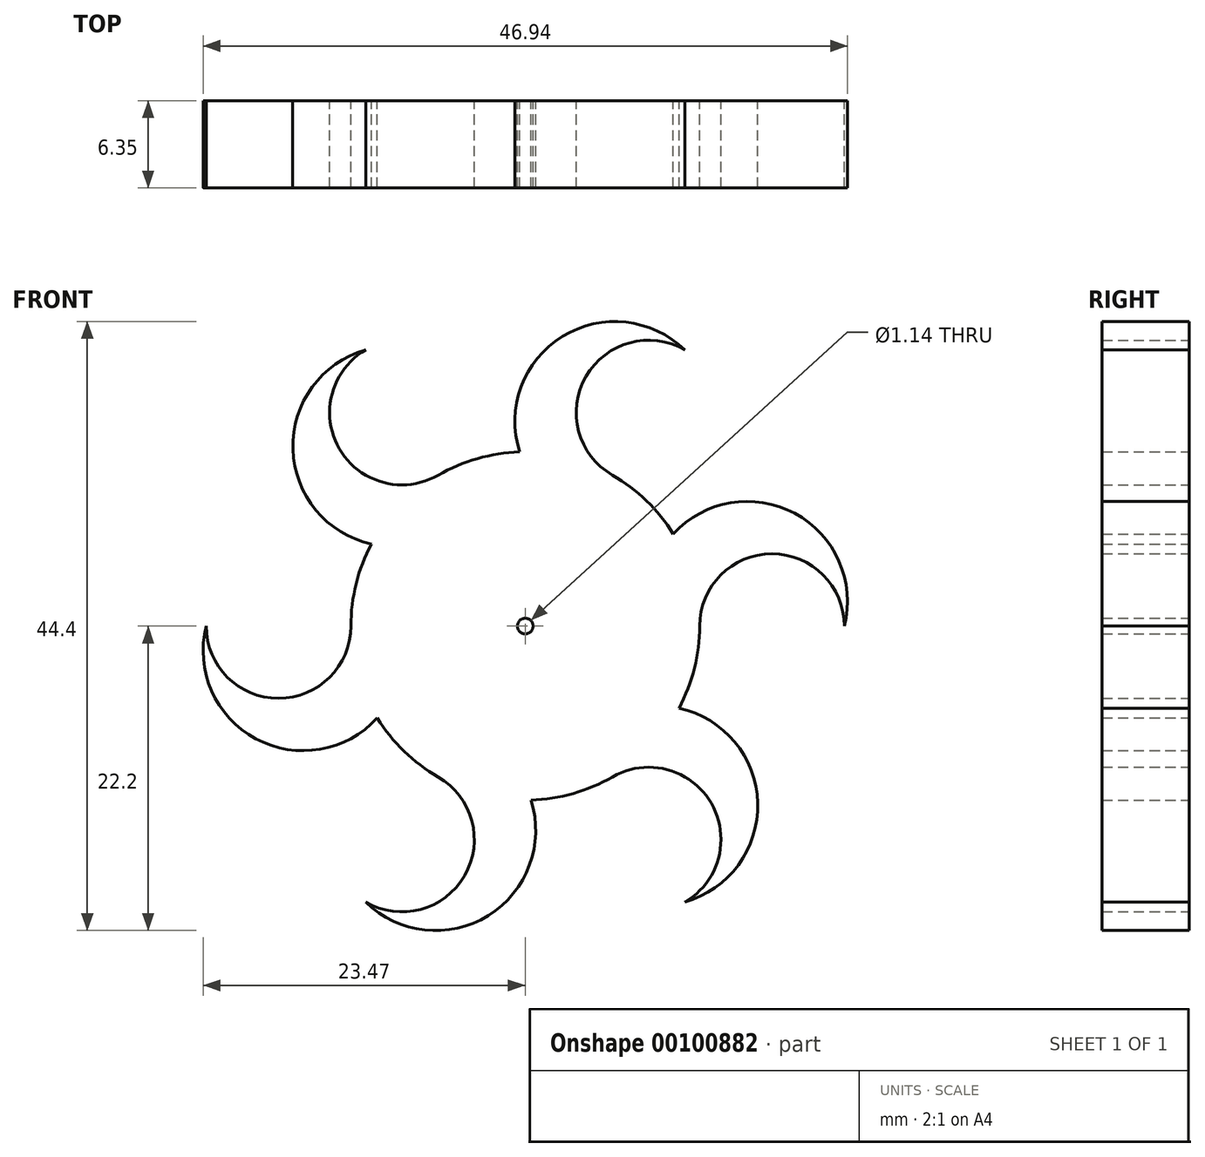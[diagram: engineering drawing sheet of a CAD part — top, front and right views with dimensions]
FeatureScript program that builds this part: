
annotation { "Feature Type Name" : "Feature", "Feature Type Description" : "" }
export const myFeature = defineFeature(function(context is Context, id is Id, definition is map)
    precondition{}
    {
        {
            var Q0;
            Q0=qCreatedBy(makeId("Front.planeOp"),FACE);
            var sketch = newSketch(context, id + "F0", { "sketchPlane" : qUnion([Q0])});
            skArc(sketch, "E0", {"start": v(10.78, 6.7) * mm, "mid": v(8.83, 9.13) * mm, "end": v(6.35, 11) * mm});
            skLineSegment(sketch, "E1", {"start": v(31, -8.23) * mm, "end": v(43.7, -8.23) * mm, "construction": true});
            skLineSegment(sketch, "E2", {"start": v(43.7, -8.23) * mm, "end": v(54.24, -8.23) * mm, "construction": true});
            skLineSegment(sketch, "E3", {"start": v(0, 0) * mm, "end": v(12.7, 0) * mm, "construction": true});
            skArc(sketch, "E4", {"start": v(12.7, 0) * mm, "mid": v(17.97, 5.27) * mm, "end": v(23.24, 0) * mm});
            skLineSegment(sketch, "E5", {"start": v(12.7, 0) * mm, "end": v(23.24, 0) * mm, "construction": true});
            skCircle(sketch, "E6", {"center": v(0, 0) * mm, "radius": 0.57 * mm});
            skArc(sketch, "E7", {"start": v(23.24, 0) * mm, "mid": v(19.63, 8.22) * mm, "end": v(10.78, 6.7) * mm});
            skLineSegment(sketch, "E8", {"start": v(16.17, 1.8) * mm, "end": v(17.97, 0) * mm, "construction": true});
            skArc(sketch, "E9.1.0", {"start": v(11.62, 20.13) * mm, "mid": v(2.7, 21.1) * mm, "end": v(-0.42, 12.7) * mm});
            skArc(sketch, "E9.1.1", {"start": v(6.35, 11) * mm, "mid": v(4.42, 18.2) * mm, "end": v(11.62, 20.13) * mm});
            skArc(sketch, "E9.2.0", {"start": v(-11.62, 20.13) * mm, "mid": v(-16.93, 12.9) * mm, "end": v(-11.2, 5.99) * mm});
            skArc(sketch, "E9.2.1", {"start": v(-6.35, 11) * mm, "mid": v(-13.55, 12.93) * mm, "end": v(-11.62, 20.13) * mm});
            skArc(sketch, "E9.3.0", {"start": v(-23.24, 0) * mm, "mid": v(-19.63, -8.22) * mm, "end": v(-10.78, -6.7) * mm});
            skArc(sketch, "E9.3.1", {"start": v(-12.7, 0) * mm, "mid": v(-17.97, -5.27) * mm, "end": v(-23.24, 0) * mm});
            skArc(sketch, "E9.4.0", {"start": v(-11.62, -20.13) * mm, "mid": v(-2.7, -21.1) * mm, "end": v(0.42, -12.7) * mm});
            skArc(sketch, "E9.4.1", {"start": v(-6.35, -11) * mm, "mid": v(-4.42, -18.2) * mm, "end": v(-11.62, -20.13) * mm});
            skArc(sketch, "E9.5.0", {"start": v(11.62, -20.13) * mm, "mid": v(16.93, -12.9) * mm, "end": v(11.2, -5.99) * mm});
            skArc(sketch, "E9.5.1", {"start": v(6.35, -11) * mm, "mid": v(13.55, -12.93) * mm, "end": v(11.62, -20.13) * mm});
            skArc(sketch, "E10.trimOffspring", {"start": v(-11.2, 5.99) * mm, "mid": v(-12.32, 3.09) * mm, "end": v(-12.7, 0) * mm});
            skArc(sketch, "E11.trimOffspring", {"start": v(-10.78, -6.7) * mm, "mid": v(-8.83, -9.13) * mm, "end": v(-6.35, -11) * mm});
            skArc(sketch, "E12.trimOffspring", {"start": v(0.42, -12.7) * mm, "mid": v(3.49, -12.21) * mm, "end": v(6.35, -11) * mm});
            skArc(sketch, "E13.trimOffspring", {"start": v(11.2, -5.99) * mm, "mid": v(12.32, -3.09) * mm, "end": v(12.7, 0) * mm});
            skArc(sketch, "E14.trimOffspring", {"start": v(-0.42, 12.7) * mm, "mid": v(-3.49, 12.21) * mm, "end": v(-6.35, 11) * mm});
            skSolve(sketch);
        }
        {
            var Q0;
            Q0 = qSketchRegion(id + "F0", true);
            extrude(context, id + "F1", {"entities" : qUnion([Q0]), "depth" : 6.35 * mm});
        }
    });
